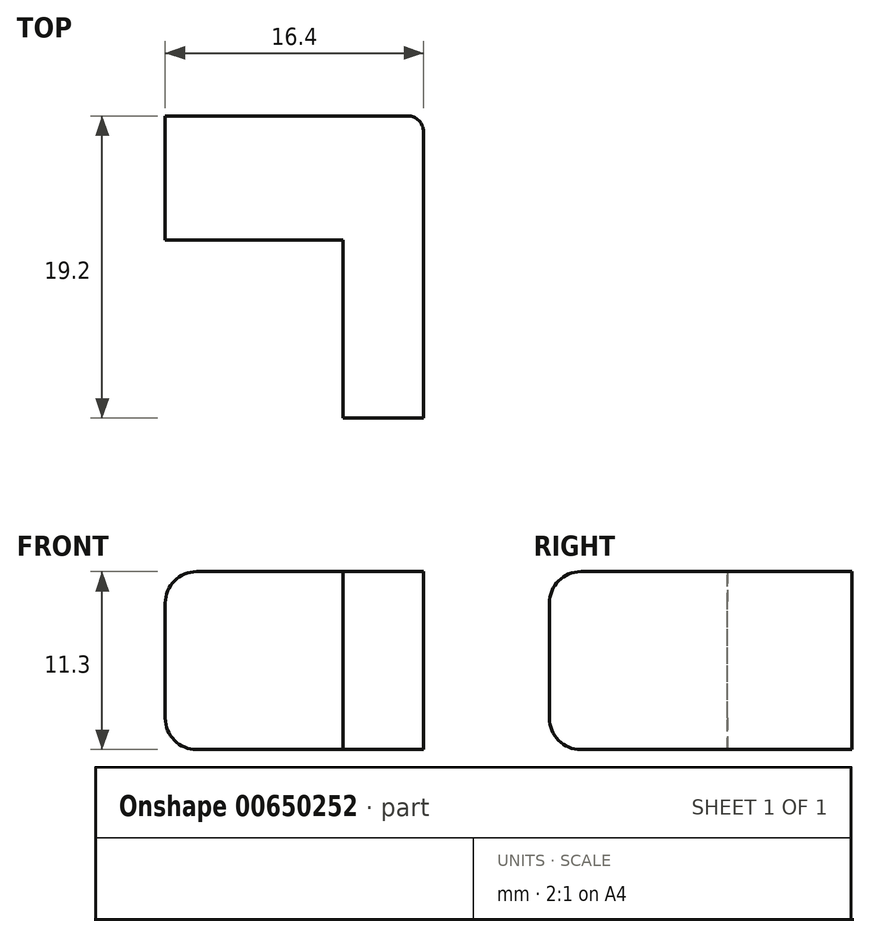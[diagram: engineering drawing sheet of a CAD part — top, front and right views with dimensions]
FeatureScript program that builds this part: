
annotation { "Feature Type Name" : "Feature", "Feature Type Description" : "" }
export const myFeature = defineFeature(function(context is Context, id is Id, definition is map)
    precondition{}
    {
        {
            var Q0;
            Q0=qCreatedBy(makeId("Top.planeOp"),FACE);
            var sketch = newSketch(context, id + "F0", { "sketchPlane" : qUnion([Q0])});
            skLineSegment(sketch, "E0.bottom", {"start": v(0, 0) * mm, "end": v(16.4, 0) * mm});
            skLineSegment(sketch, "E0.top", {"start": v(0, 19.2) * mm, "end": v(16.4, 19.2) * mm});
            skLineSegment(sketch, "E0.left", {"start": v(0, 0) * mm, "end": v(0, 19.2) * mm});
            skLineSegment(sketch, "E0.right", {"start": v(16.4, 0) * mm, "end": v(16.4, 19.2) * mm});
            skSolve(sketch);
        }
        {
            var Q0;
            Q0=makeQuery(id+"F0.imprint","IMPRINT",FACE,{"disambiguationData":[TD([[makeQuery(id+"F0.imprint","IMPRINT",EDGE,{"derivedFrom":sQuery(id+"F0.wireOp",EDGE,"E0.bottom")}),1.0]])]});
            extrude(context, id + "F1", {"entities" : qUnion([Q0]), "depth" : 11.3 * mm, "offsetDistance" : 25 * mm});
        }
        {
            var Q0;
            Q0=makeQuery(id+"F1.opExtrude","CAP_FACE",FACE,{"disambiguationData":[OSD([sQuery(id+"F0.wireOp",EDGE,"E0.bottom"),sQuery(id+"F0.wireOp",EDGE,"E0.top"),sQuery(id+"F0.wireOp",EDGE,"E0.left"),sQuery(id+"F0.wireOp",EDGE,"E0.right")])],"isStart":false});
            var sketch = newSketch(context, id + "F2", { "sketchPlane" : qUnion([Q0])});
            skLineSegment(sketch, "E1.bottom", {"start": v(0, 0) * mm, "end": v(11.3, 0) * mm});
            skLineSegment(sketch, "E1.top", {"start": v(0, 11.3) * mm, "end": v(11.3, 11.3) * mm});
            skLineSegment(sketch, "E1.left", {"start": v(0, 0) * mm, "end": v(0, 11.3) * mm});
            skLineSegment(sketch, "E1.right", {"start": v(11.3, 0) * mm, "end": v(11.3, 11.3) * mm});
            skSolve(sketch);
        }
        {
            var Q0;
            Q0=makeQuery(id+"F2.imprint","IMPRINT",FACE,{"disambiguationData":[TD([[makeQuery(id+"F2.imprint","IMPRINT",EDGE,{"derivedFrom":sQuery(id+"F2.wireOp",EDGE,"E1.bottom")}),1.0]])]});
            extrude(context, id + "F3", {"entities" : qUnion([Q0]), "operationType" : NewBodyOperationType.REMOVE, "oppositeDirection" : true, "depth" : 25 * mm, "offsetDistance" : 25 * mm});
        }
        {
            var Q0;
            Q0=makeQuery(id+"F1.opExtrude","CAP_EDGE",EDGE,{"disambiguationData":[OSD([sQuery(id+"F0.wireOp",EDGE,"E0.bottom")])],"isStart":true});
            var Q1;
            Q1=makeQuery(id+"F1.opExtrude","CAP_EDGE",EDGE,{"disambiguationData":[OSD([sQuery(id+"F0.wireOp",EDGE,"E0.left")])],"isStart":true});
            var Q2;
            Q2=makeQuery(id+"F1.opExtrude","CAP_EDGE",EDGE,{"disambiguationData":[OSD([sQuery(id+"F0.wireOp",EDGE,"E0.bottom")])],"isStart":false});
            var Q3;
            Q3=makeQuery(id+"F1.opExtrude","CAP_EDGE",EDGE,{"disambiguationData":[OSD([sQuery(id+"F0.wireOp",EDGE,"E0.left")])],"isStart":false});
            fillet(context, id + "F4", {"entities" : qUnion([Q0, Q1, Q2, Q3]), "radius" : 2 * mm, "tangentPropagation" : true, "allowEdgeOverflow" : false});
        }
        {
            var Q0;
            Q0=makeQuery(id+"F1.opExtrude","SWEPT_EDGE",EDGE,{"disambiguationData":[OSD([sQuery(id+"F0.wireOp",EDGE,"E0.top"),sQuery(id+"F0.wireOp",EDGE,"E0.right")])]});
            fillet(context, id + "F5", {"entities" : qUnion([Q0]), "radius" : 1 * mm, "tangentPropagation" : true, "allowEdgeOverflow" : false});
        }
    });
